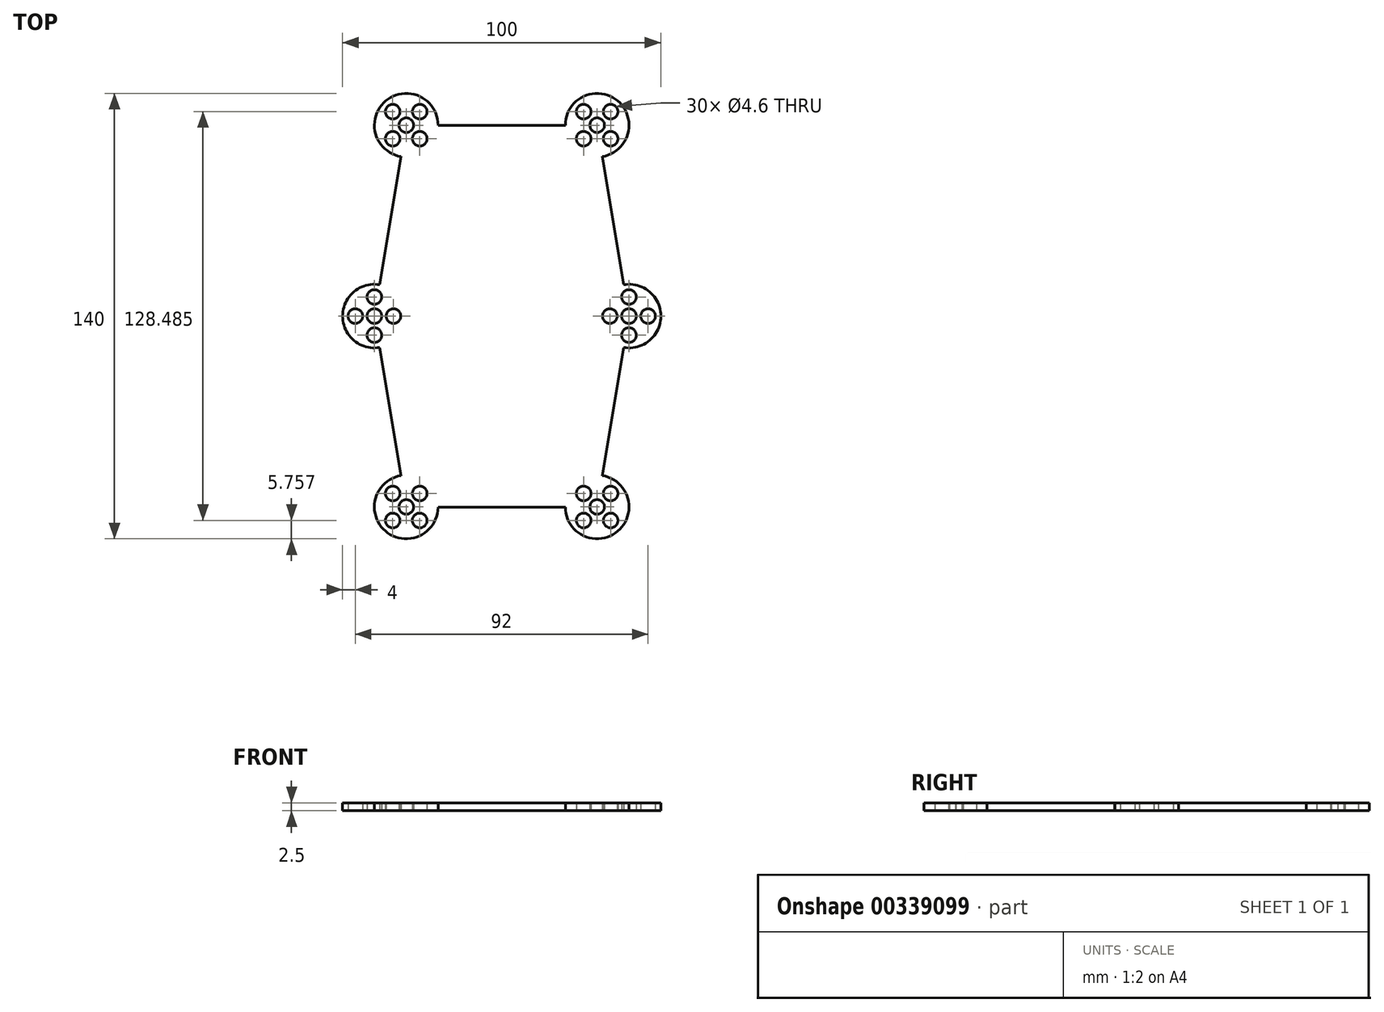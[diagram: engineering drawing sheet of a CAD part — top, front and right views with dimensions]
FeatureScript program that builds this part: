
annotation { "Feature Type Name" : "Feature", "Feature Type Description" : "" }
export const myFeature = defineFeature(function(context is Context, id is Id, definition is map)
    precondition{}
    {
        {
            var Q0;
            Q0=qCreatedBy(makeId("Top.planeOp"),FACE);
            var sketch = newSketch(context, id + "F0", { "sketchPlane" : qUnion([Q0])});
            skCircle(sketch, "E0", {"center": v(-46, 0) * mm, "radius": 2.3 * mm});
            skCircle(sketch, "E1", {"center": v(-40, 0) * mm, "radius": 2.3 * mm});
            skCircle(sketch, "E2", {"center": v(-34, 0) * mm, "radius": 2.3 * mm});
            skCircle(sketch, "E3", {"center": v(-40, 6) * mm, "radius": 2.3 * mm});
            skCircle(sketch, "E4", {"center": v(-40, -6) * mm, "radius": 2.3 * mm});
            skArc(sketch, "E5", {"start": v(-38.36, 9.86) * mm, "mid": v(-50, 0) * mm, "end": v(-38.36, -9.86) * mm});
            skCircle(sketch, "E6", {"center": v(34, 0) * mm, "radius": 2.3 * mm});
            skCircle(sketch, "E7", {"center": v(40, 0) * mm, "radius": 2.3 * mm});
            skCircle(sketch, "E8", {"center": v(46, 0) * mm, "radius": 2.3 * mm});
            skCircle(sketch, "E9", {"center": v(40, 6) * mm, "radius": 2.3 * mm});
            skCircle(sketch, "E10", {"center": v(40, -6) * mm, "radius": 2.3 * mm});
            skArc(sketch, "E11", {"start": v(38.36, -9.86) * mm, "mid": v(50, 0) * mm, "end": v(38.36, 9.86) * mm});
            skCircle(sketch, "E12", {"center": v(-34.24, 64.24) * mm, "radius": 2.3 * mm});
            skCircle(sketch, "E13", {"center": v(-30, 60) * mm, "radius": 2.3 * mm});
            skCircle(sketch, "E14", {"center": v(-25.76, 55.76) * mm, "radius": 2.3 * mm});
            skCircle(sketch, "E15", {"center": v(-25.76, 64.24) * mm, "radius": 2.3 * mm});
            skCircle(sketch, "E16", {"center": v(-34.24, 55.76) * mm, "radius": 2.3 * mm});
            skArc(sketch, "E17", {"start": v(-20, 60) * mm, "mid": v(-36.46, 67.63) * mm, "end": v(-31.64, 50.14) * mm});
            skLineSegment(sketch, "E18.0", {"start": v(-34.24, 64.24) * mm, "end": v(-25.76, 55.76) * mm, "construction": true});
            skLineSegment(sketch, "E19.0", {"start": v(-34.24, 55.76) * mm, "end": v(-25.76, 64.24) * mm, "construction": true});
            skCircle(sketch, "E20", {"center": v(-34.24, -55.76) * mm, "radius": 2.3 * mm});
            skCircle(sketch, "E21", {"center": v(-30, -60) * mm, "radius": 2.3 * mm});
            skCircle(sketch, "E22", {"center": v(-25.76, -64.24) * mm, "radius": 2.3 * mm});
            skCircle(sketch, "E23", {"center": v(-25.76, -55.76) * mm, "radius": 2.3 * mm});
            skCircle(sketch, "E24", {"center": v(-34.24, -64.24) * mm, "radius": 2.3 * mm});
            skArc(sketch, "E25", {"start": v(-31.64, -50.14) * mm, "mid": v(-36.52, -67.59) * mm, "end": v(-20, -60.14) * mm});
            skLineSegment(sketch, "E26.0", {"start": v(-34.24, -55.76) * mm, "end": v(-25.76, -64.24) * mm, "construction": true});
            skLineSegment(sketch, "E27.0", {"start": v(-34.24, -64.24) * mm, "end": v(-25.76, -55.76) * mm, "construction": true});
            skCircle(sketch, "E28", {"center": v(25.76, -55.76) * mm, "radius": 2.3 * mm});
            skCircle(sketch, "E29", {"center": v(30, -60) * mm, "radius": 2.3 * mm});
            skCircle(sketch, "E30", {"center": v(34.24, -64.24) * mm, "radius": 2.3 * mm});
            skCircle(sketch, "E31", {"center": v(34.24, -55.76) * mm, "radius": 2.3 * mm});
            skCircle(sketch, "E32", {"center": v(25.76, -64.24) * mm, "radius": 2.3 * mm});
            skArc(sketch, "E33", {"start": v(20, -60.03) * mm, "mid": v(36.47, -67.62) * mm, "end": v(31.64, -50.14) * mm});
            skLineSegment(sketch, "E34.0", {"start": v(25.76, -55.76) * mm, "end": v(34.24, -64.24) * mm, "construction": true});
            skLineSegment(sketch, "E35.0", {"start": v(25.76, -64.24) * mm, "end": v(34.24, -55.76) * mm, "construction": true});
            skCircle(sketch, "E36", {"center": v(25.76, 64.24) * mm, "radius": 2.3 * mm});
            skCircle(sketch, "E37", {"center": v(30, 60) * mm, "radius": 2.3 * mm});
            skCircle(sketch, "E38", {"center": v(34.24, 55.76) * mm, "radius": 2.3 * mm});
            skCircle(sketch, "E39", {"center": v(34.24, 64.24) * mm, "radius": 2.3 * mm});
            skCircle(sketch, "E40", {"center": v(25.76, 55.76) * mm, "radius": 2.3 * mm});
            skArc(sketch, "E41", {"start": v(31.64, 50.14) * mm, "mid": v(36.46, 67.63) * mm, "end": v(20, 60) * mm});
            skLineSegment(sketch, "E42.0", {"start": v(25.76, 64.24) * mm, "end": v(34.24, 55.76) * mm, "construction": true});
            skLineSegment(sketch, "E43.0", {"start": v(25.76, 55.76) * mm, "end": v(34.24, 64.24) * mm, "construction": true});
            skLineSegment(sketch, "E44", {"start": v(-30.16, -60.17) * mm, "end": v(-29.83, -60.17) * mm});
            skLineSegment(sketch, "E45", {"start": v(-20, 60) * mm, "end": v(20, 60) * mm});
            skLineSegment(sketch, "E46.trimOffspring", {"start": v(-31.64, 50.14) * mm, "end": v(-38.36, 9.86) * mm});
            skLineSegment(sketch, "E47.trimOffspring", {"start": v(31.64, 50.14) * mm, "end": v(38.36, 9.86) * mm});
            skLineSegment(sketch, "E48.trimOffspring", {"start": v(31.64, -50.14) * mm, "end": v(38.36, -9.86) * mm});
            skLineSegment(sketch, "E49.trimOffspring", {"start": v(-20, -60.14) * mm, "end": v(20, -60.03) * mm});
            skLineSegment(sketch, "E50.trimOffspring", {"start": v(-38.36, -9.86) * mm, "end": v(-31.64, -50.14) * mm});
            skSolve(sketch);
        }
        {
            var Q0;
            Q0=makeQuery(id+"F0.imprint","IMPRINT",FACE,{"disambiguationData":[TD([[makeQuery(id+"F0.imprint","IMPRINT",EDGE,{"derivedFrom":sQuery(id+"F0.wireOp",EDGE,"E0")}),-1.0]])]});
            extrude(context, id + "F1", {"entities" : qUnion([Q0]), "depth" : 2.5 * mm});
        }
    });
